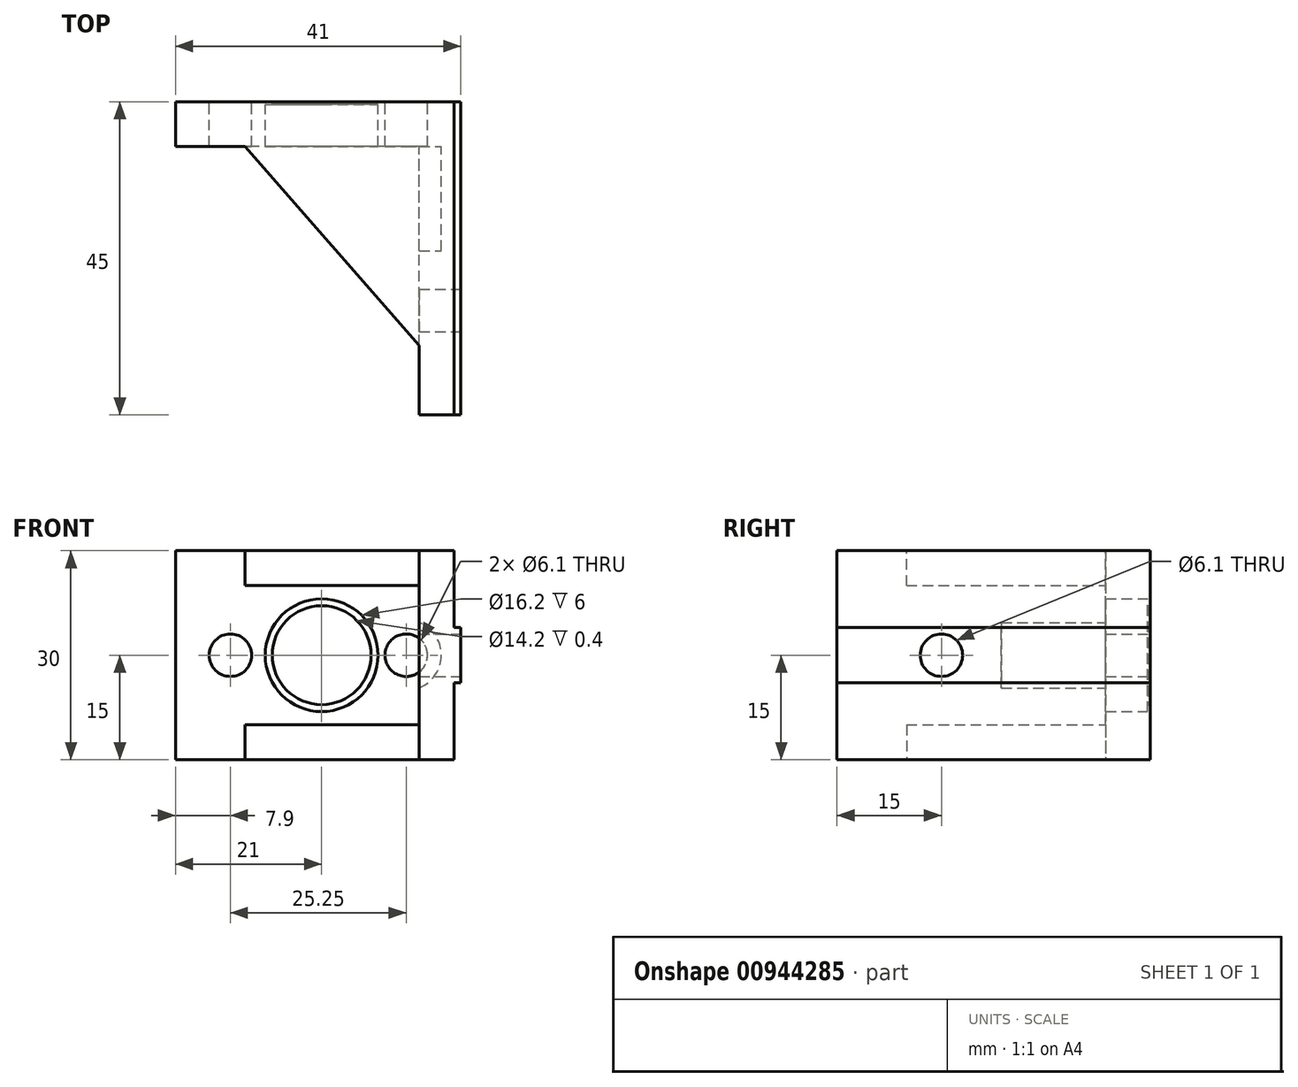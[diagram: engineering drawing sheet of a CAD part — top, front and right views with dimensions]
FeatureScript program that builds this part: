
annotation { "Feature Type Name" : "Feature", "Feature Type Description" : "" }
export const myFeature = defineFeature(function(context is Context, id is Id, definition is map)
    precondition{}
    {
        {
            var Q0;
            Q0=qCreatedBy(makeId("Front.planeOp"),FACE);
            var sketch = newSketch(context, id + "F0", { "sketchPlane" : qUnion([Q0])});
            skPoint(sketch, "E0.middle", {"position": v(0, 0) * mm});
            skCircle(sketch, "E1", {"center": v(-13.1, 0) * mm, "radius": 3.05 * mm});
            skCircle(sketch, "E2", {"center": v(0, 0) * mm, "radius": 8.1 * mm});
            skLineSegment(sketch, "E3.bottom", {"start": v(14, 15) * mm, "end": v(19, 15) * mm});
            skLineSegment(sketch, "E3.top", {"start": v(14, -15) * mm, "end": v(19, -15) * mm});
            skLineSegment(sketch, "E3.left", {"start": v(14, 15) * mm, "end": v(14, -15) * mm});
            skLineSegment(sketch, "E3.right", {"start": v(19, 15) * mm, "end": v(19, -15) * mm});
            skLineSegment(sketch, "E4.bottom", {"start": v(14, 15) * mm, "end": v(-21, 15) * mm});
            skLineSegment(sketch, "E4.top", {"start": v(14, -15) * mm, "end": v(-21, -15) * mm});
            skLineSegment(sketch, "E4.right", {"start": v(-21, 15) * mm, "end": v(-21, -15) * mm});
            skCircle(sketch, "E5", {"center": v(12.15, 0) * mm, "radius": 3.05 * mm});
            skSolve(sketch);
        }
        {
            var Q0;
            Q0=makeQuery(id+"F0.imprint","IMPRINT",FACE,{"disambiguationData":[TD([[makeQuery(id+"F0.imprint","IMPRINT",EDGE,{"derivedFrom":sQuery(id+"F0.wireOp",EDGE,"E2")}),-1.0]])]});
            var Q1;
            {var subQ2=sQuery(id+"F0.wireOp",EDGE,"E3.bottom");Q1=makeQuery(id+"F0.imprint","IMPRINT",FACE,{"disambiguationData":[TD([[makeQuery(id+"F0.imprint","IMPRINT",EDGE,{"derivedFrom":subQ2}),-1.0]])]});}
            extrude(context, id + "F1", {"entities" : qUnion([Q0, Q1]), "depth" : 6.4 * mm, "offsetDistance" : 25 * mm});
        }
        {
            var Q0;
            Q0=makeQuery(id+"F0.imprint","IMPRINT",FACE,{"disambiguationData":[TD([[makeQuery(id+"F0.imprint","IMPRINT",EDGE,{"derivedFrom":sQuery(id+"F0.wireOp",EDGE,"E3.bottom")}),-1.0]])]});
            var Q1;
            {var subQ0=sQuery(id+"F0.wireOp",EDGE,"E5");var subQ1=sQuery(id+"F0.wireOp",EDGE,"E3.left");var subQ2=makeQuery(id+"F0.imprint","INTERSECT",VERTEX,{"disambiguationData":[OD(0.0)],"derivedFrom":[subQ1,subQ0]});Q1=makeQuery(id+"F0.imprint","IMPRINT",FACE,{"disambiguationData":[TD([[makeQuery(id+"F0.imprint","IMPRINT",EDGE,{"disambiguationData":[TD([[subQ2,-1.0]])],"derivedFrom":subQ1}),1.0]])]});}
            extrude(context, id + "F2", {"entities" : qUnion([Q0, Q1]), "operationType" : NewBodyOperationType.ADD, "depth" : 45 * mm, "offsetDistance" : 25 * mm, "hasSecondDirection" : true, "secondDirectionOppositeDirection" : false, "secondDirectionDepth" : 5 * mm});
        }
        {
            var Q0;
            {var subQ0=sQuery(id+"F0.wireOp",EDGE,"C86Frku9-35ry-Nnsr-swNd-JGyjtVE7eqIW");Q0=makeQuery(id+"FHz6JOgAJKxZFWy_1.boolean.opBoolean","MERGE",FACE,{"derivedFrom":[makeQuery(id+"F1.opExtrude","CAP_FACE",FACE,{"disambiguationData":[OSD([sQuery(id+"F0.wireOp",EDGE,"E2"),subQ0])],"isStart":true}),makeQuery(id+"FHz6JOgAJKxZFWy_1.opExtrude","CAP_FACE",FACE,{"disambiguationData":[OSD([sQuery(id+"F0.wireOp",EDGE,"E0.bottom"),sQuery(id+"F0.wireOp",EDGE,"E0.top"),sQuery(id+"F0.wireOp",EDGE,"E0.left"),sQuery(id+"F0.wireOp",EDGE,"E0.right"),sQuery(id+"F0.wireOp",EDGE,"E1"),sQuery(id+"F0.wireOp",EDGE,"6cb2f09e-4676-46e8-bcb4-572f2d68a4c60.MirrorC"),subQ0,sQuery(id+"F0.wireOp",EDGE,"LP3tDRcQ-mJ9R-RbPk-Qv1U-xYvXF342wEAe"),sQuery(id+"F0.wireOp",EDGE,"fcef568d-7fc3-4169-8c44-c390feec9811.filletArc"),sQuery(id+"F0.wireOp",EDGE,"0bf67bc2-62a5-4791-a951-983d11034ea5.filletArc"),sQuery(id+"F0.wireOp",EDGE,"a1945099-096e-447e-bc1c-ab5cae43a46e0.MirrorCS"),sQuery(id+"F0.wireOp",EDGE,"e7613415-c0dd-44c2-a091-62de6971341e0.MirrorCS"),sQuery(id+"F0.wireOp",EDGE,"568613a7-9c33-49a0-9674-28169e1cce0e0.MirrorCS"),sQuery(id+"F0.wireOp",EDGE,"278f71a7-0881-42c8-984d-851adb8181b20.MirrorCS"),sQuery(id+"F0.wireOp",EDGE,"d51d1d82-35a3-4542-a6ef-0a179e79d5560.MirrorCS"),sQuery(id+"F0.wireOp",EDGE,"fc348f83-c17f-4d2a-976c-bcf134866c6b0.MirrorCS"),sQuery(id+"F0.wireOp",EDGE,"7480bcef-4817-4377-8283-0c3d8621cf620.MirrorCS"),sQuery(id+"F0.wireOp",EDGE,"9ec5c487-3746-435e-b199-95de8daa40a20.MirrorCS"),sQuery(id+"F0.wireOp",EDGE,"8ba82cc5-7c4e-43a8-960a-3daafe53bb050.MirrorCS")])],"isStart":true})]});}
            var sketch = newSketch(context, id + "F3", { "sketchPlane" : qUnion([Q0])});
            skCircle(sketch, "E6", {"center": v(0, 0) * mm, "radius": 7.1 * mm});
            skSolve(sketch);
        }
        {
            var Q0;
            Q0=makeQuery(id+"F3.imprint","IMPRINT",FACE,{"disambiguationData":[TD([[makeQuery(id+"F3.imprint","IMPRINT",EDGE,{"derivedFrom":sQuery(id+"F3.wireOp",EDGE,"E6")}),-1.0]])]});
            extrude(context, id + "F4", {"entities" : qUnion([Q0]), "operationType" : NewBodyOperationType.ADD, "oppositeDirection" : true, "depth" : 0.4 * mm, "offsetDistance" : 25 * mm});
        }
        {
            var Q0;
            {var subQ0=sQuery(id+"F0.wireOp",EDGE,"E3.top");Q0=makeQuery(id+"F2.boolean.opBoolean","MERGE",FACE,{"derivedFrom":[makeQuery(id+"FHz6JOgAJKxZFWy_1.opExtrude","SWEPT_FACE",FACE,{"disambiguationData":[OSD([sQuery(id+"F0.wireOp",EDGE,"dl1EBA6h-zHJt-CsKo-ewyl-A43VLyflkz5p"),subQ0])]}),makeQuery(id+"F2.opExtrude","SWEPT_FACE",FACE,{"disambiguationData":[OSD([subQ0])]})]});}
            var sketch = newSketch(context, id + "F5", { "sketchPlane" : qUnion([Q0])});
            skLineSegment(sketch, "E7", {"start": v(14, 6.4) * mm, "end": v(14, 35) * mm});
            skLineSegment(sketch, "E8", {"start": v(14, 35) * mm, "end": v(-11, 6.4) * mm});
            skLineSegment(sketch, "E9", {"start": v(-11, 6.4) * mm, "end": v(14, 6.4) * mm});
            skSolve(sketch);
        }
        {
            var Q0;
            Q0 = qSketchRegion(id + "F5", true);
            extrude(context, id + "F6", {"entities" : qUnion([Q0]), "operationType" : NewBodyOperationType.ADD, "oppositeDirection" : true, "depth" : 5 * mm, "offsetDistance" : 25 * mm});
        }
        {
            var Q0;
            {var subQ0=sQuery(id+"F0.wireOp",EDGE,"E3.bottom");Q0=makeQuery(id+"F2.boolean.opBoolean","MERGE",FACE,{"derivedFrom":[makeQuery(id+"FHz6JOgAJKxZFWy_1.opExtrude","SWEPT_FACE",FACE,{"disambiguationData":[OSD([sQuery(id+"F0.wireOp",EDGE,"cO2YNnPV-bPgm-7vOo-iThm-KKIT8V0MzUBl"),subQ0])]}),makeQuery(id+"F2.opExtrude","SWEPT_FACE",FACE,{"disambiguationData":[OSD([subQ0])]})]});}
            var sketch = newSketch(context, id + "F7", { "sketchPlane" : qUnion([Q0])});
            skLineSegment(sketch, "E10", {"start": v(14, -6.4) * mm, "end": v(14, -35) * mm});
            skLineSegment(sketch, "E11", {"start": v(14, -35) * mm, "end": v(-11, -6.4) * mm});
            skLineSegment(sketch, "E12", {"start": v(-11, -6.4) * mm, "end": v(14, -6.4) * mm});
            skSolve(sketch);
        }
        {
            var Q0;
            Q0 = qSketchRegion(id + "F7", true);
            extrude(context, id + "F8", {"entities" : qUnion([Q0]), "operationType" : NewBodyOperationType.ADD, "oppositeDirection" : true, "depth" : 5 * mm, "offsetDistance" : 25 * mm});
        }
        {
            var Q0;
            Q0=makeQuery(id+"F2.opExtrude","SWEPT_FACE",FACE,{"disambiguationData":[OSD([sQuery(id+"F0.wireOp",EDGE,"E3.right")])]});
            var sketch = newSketch(context, id + "F9", { "sketchPlane" : qUnion([Q0])});
            skCircle(sketch, "E13", {"center": v(-30, 0) * mm, "radius": 3.05 * mm});
            skSolve(sketch);
        }
        {
            var Q0;
            Q0=makeQuery(id+"F9.imprint","IMPRINT",FACE,{"disambiguationData":[TD([[makeQuery(id+"F9.imprint","IMPRINT",EDGE,{"derivedFrom":sQuery(id+"F9.wireOp",EDGE,"E13")}),1.0]])]});
            extrude(context, id + "F10", {"entities" : qUnion([Q0]), "operationType" : NewBodyOperationType.REMOVE, "oppositeDirection" : true, "depth" : 25 * mm, "offsetDistance" : 25 * mm});
        }
        {
            var Q0;
            Q0=makeQuery(id+"F2.opExtrude","SWEPT_FACE",FACE,{"disambiguationData":[OSD([sQuery(id+"F0.wireOp",EDGE,"E3.right")])]});
            var sketch = newSketch(context, id + "F11", { "sketchPlane" : qUnion([Q0])});
            skLineSegment(sketch, "E14.bottom", {"start": v(0, -3.95) * mm, "end": v(-45, -3.95) * mm});
            skLineSegment(sketch, "E14.top", {"start": v(0, 3.95) * mm, "end": v(-45, 3.95) * mm});
            skLineSegment(sketch, "E14.left", {"start": v(0, -3.95) * mm, "end": v(0, 3.95) * mm});
            skLineSegment(sketch, "E14.right", {"start": v(-45, -3.95) * mm, "end": v(-45, 3.95) * mm});
            skPoint(sketch, "E14.middle", {"position": v(-22.5, 0) * mm});
            skPoint(sketch, "E14.middle.positionSnap0", {"position": v(-22.5, 15) * mm});
            skPoint(sketch, "E14.centerSnap0", {"position": v(-22.5, 15) * mm});
            skSolve(sketch);
        }
        {
            var Q0;
            Q0=makeQuery(id+"F11.imprint","IMPRINT",FACE,{"disambiguationData":[TD([[makeQuery(id+"F11.imprint","IMPRINT",EDGE,{"derivedFrom":sQuery(id+"F11.wireOp",EDGE,"E14.bottom")}),-1.0]])]});
            extrude(context, id + "F12", {"entities" : qUnion([Q0]), "operationType" : NewBodyOperationType.ADD, "depth" : 1 * mm, "offsetDistance" : 25 * mm});
        }
        {
            var Q0;
            Q0=makeQuery(id+"F1.opExtrude","CAP_FACE",FACE,{"disambiguationData":[OSD([sQuery(id+"F0.wireOp",EDGE,"E1"),sQuery(id+"F0.wireOp",EDGE,"E2"),sQuery(id+"F0.wireOp",EDGE,"E3.bottom"),sQuery(id+"F0.wireOp",EDGE,"E3.top"),sQuery(id+"F0.wireOp",EDGE,"E3.right"),sQuery(id+"F0.wireOp",EDGE,"E4.bottom"),sQuery(id+"F0.wireOp",EDGE,"E4.top"),sQuery(id+"F0.wireOp",EDGE,"E4.right"),sQuery(id+"F0.wireOp",EDGE,"E5")])],"isStart":false});
            var sketch = newSketch(context, id + "F13", { "sketchPlane" : qUnion([Q0])});
            skCircle(sketch, "E15", {"center": v(12.15, 0) * mm, "radius": 5.05 * mm});
            skSolve(sketch);
        }
        {
            var Q0;
            {var subQ4=sQuery(id+"F0.wireOp",EDGE,"E5");var subQ9=makeQuery(id+"F1.opExtrude","CAP_EDGE",EDGE,{"disambiguationData":[OSD([subQ4])],"isStart":false});Q0=makeQuery(id+"F13.imprint","IMPRINT",FACE,{"disambiguationData":[TD([[makeQuery(id+"F13.imprint","IMPRINT",EDGE,{"derivedFrom":subQ9}),-1.0]])]});}
            var Q1;
            {var subQ2=sQuery(id+"F0.wireOp",EDGE,"E5");var subQ8=makeQuery(id+"F1.opExtrude","CAP_EDGE",EDGE,{"disambiguationData":[OSD([subQ2])],"isStart":false});Q1=makeQuery(id+"F13.imprint","IMPRINT",FACE,{"disambiguationData":[TD([[makeQuery(id+"F13.imprint","IMPRINT",EDGE,{"derivedFrom":subQ8}),1.0]])]});}
            extrude(context, id + "F14", {"entities" : qUnion([Q0, Q1]), "operationType" : NewBodyOperationType.REMOVE, "depth" : 15 * mm, "offsetDistance" : 25 * mm});
        }
        {
            var Q0;
            {var subQ0=sQuery(id+"F0.wireOp",EDGE,"E5");var subQ1=sQuery(id+"F0.wireOp",EDGE,"E3.left");var subQ2=makeQuery(id+"F0.imprint","INTERSECT",VERTEX,{"disambiguationData":[OD(0.0)],"derivedFrom":[subQ1,subQ0]});Q0=makeQuery(id+"F0.imprint","IMPRINT",FACE,{"disambiguationData":[TD([[makeQuery(id+"F0.imprint","IMPRINT",EDGE,{"disambiguationData":[TD([[subQ2,-1.0]])],"derivedFrom":subQ1}),-1.0]])]});}
            var Q1;
            {var subQ0=sQuery(id+"F0.wireOp",EDGE,"E5");var subQ1=sQuery(id+"F0.wireOp",EDGE,"E3.left");var subQ2=makeQuery(id+"F0.imprint","INTERSECT",VERTEX,{"disambiguationData":[OD(0.0)],"derivedFrom":[subQ1,subQ0]});Q1=makeQuery(id+"F0.imprint","IMPRINT",FACE,{"disambiguationData":[TD([[makeQuery(id+"F0.imprint","IMPRINT",EDGE,{"disambiguationData":[TD([[subQ2,-1.0]])],"derivedFrom":subQ1}),1.0]])]});}
            extrude(context, id + "F15", {"entities" : qUnion([Q0, Q1]), "operationType" : NewBodyOperationType.REMOVE, "depth" : 10 * mm, "offsetDistance" : 25 * mm});
        }
    });
